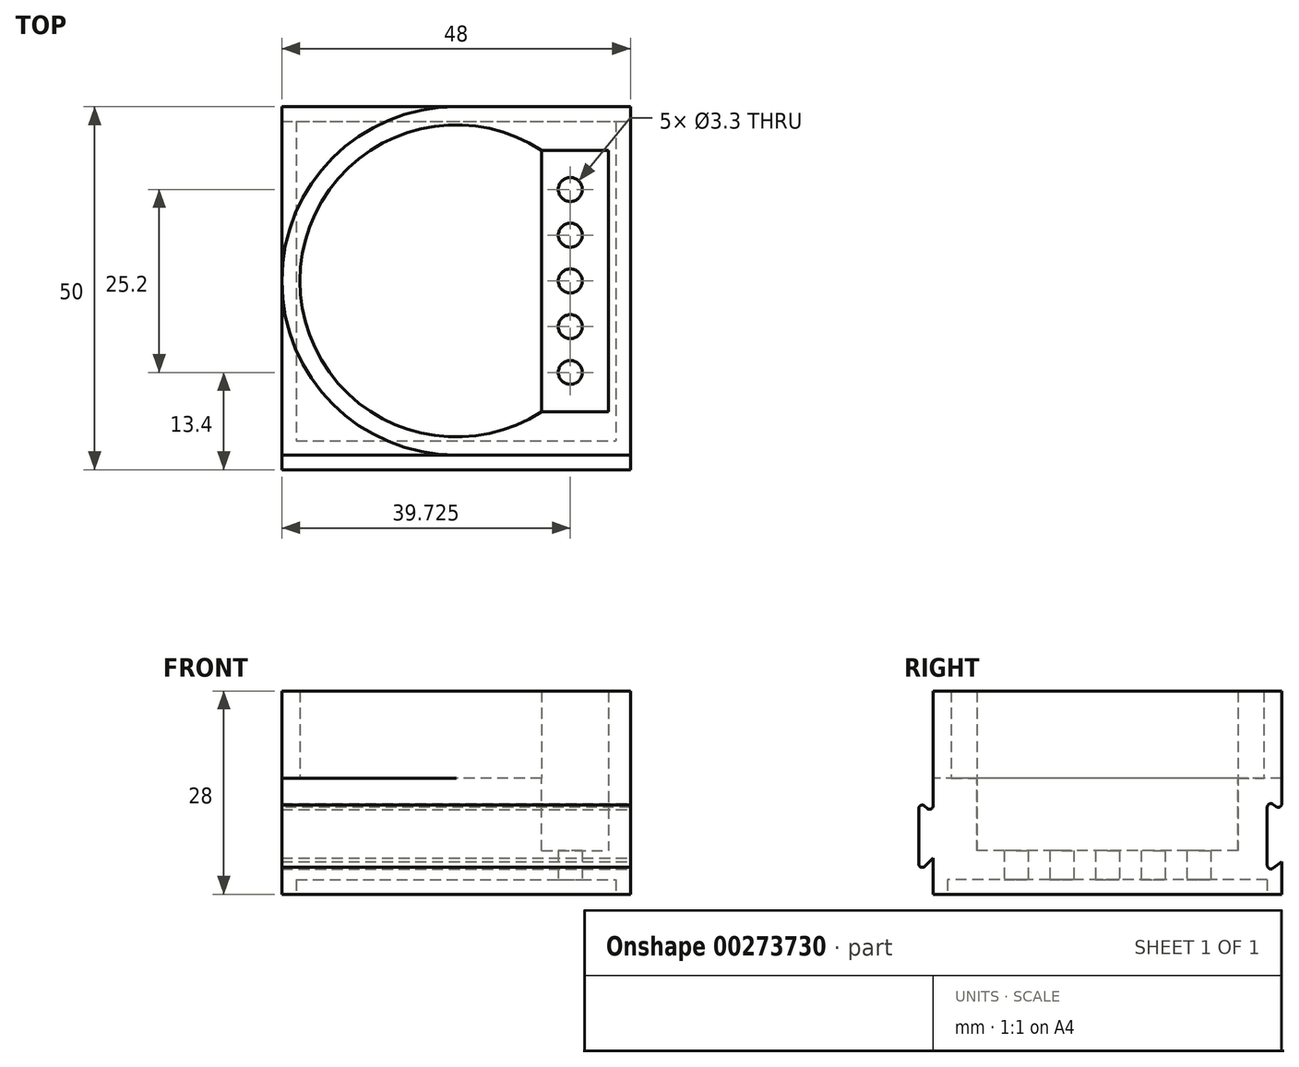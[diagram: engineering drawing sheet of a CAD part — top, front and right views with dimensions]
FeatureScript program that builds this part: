
annotation { "Feature Type Name" : "Feature", "Feature Type Description" : "" }
export const myFeature = defineFeature(function(context is Context, id is Id, definition is map)
    precondition{}
    {
        {
            var Q0;
            Q0=qCreatedBy(makeId("Top.planeOp"),FACE);
            var sketch = newSketch(context, id + "F0", { "sketchPlane" : qUnion([Q0])});
            skCircle(sketch, "E0", {"center": v(0, 0) * mm, "radius": 21.5 * mm});
            skCircle(sketch, "E1", {"center": v(0, 0) * mm, "radius": 24 * mm});
            skLineSegment(sketch, "E2.bottom", {"start": v(-24, 24) * mm, "end": v(24, 24) * mm});
            skLineSegment(sketch, "E2.top", {"start": v(-24, -24) * mm, "end": v(24, -24) * mm});
            skLineSegment(sketch, "E2.left", {"start": v(-24, 24) * mm, "end": v(-24, -24) * mm});
            skLineSegment(sketch, "E2.right", {"start": v(24, 24) * mm, "end": v(24, -24) * mm});
            skPoint(sketch, "E3", {"position": v(0, 24) * mm});
            skPoint(sketch, "E4", {"position": v(-24, 0) * mm});
            skLineSegment(sketch, "E5.bottom", {"start": v(11.76, 18) * mm, "end": v(20.96, 18) * mm});
            skLineSegment(sketch, "E5.top", {"start": v(11.76, -18) * mm, "end": v(20.96, -18) * mm});
            skLineSegment(sketch, "E5.left", {"start": v(11.76, 18) * mm, "end": v(11.76, -18) * mm});
            skLineSegment(sketch, "E5.right", {"start": v(20.96, 18) * mm, "end": v(20.96, -18) * mm});
            skLineSegment(sketch, "E6", {"start": v(20.96, -18) * mm, "end": v(20.96, -24) * mm, "construction": true});
            skLineSegment(sketch, "E7", {"start": v(20.96, 18) * mm, "end": v(20.96, 24) * mm, "construction": true});
            skCircle(sketch, "E8", {"center": v(0, 0) * mm, "radius": 20.15 * mm, "construction": true});
            skSolve(sketch);
        }
        {
            var Q0;
            Q0=makeQuery(id+"F0.imprint","IMPRINT",FACE,{"disambiguationData":[TD([[makeQuery(id+"F0.imprint","IMPRINT",EDGE,{"derivedFrom":sQuery(id+"F0.wireOp",EDGE,"E1")}),-1.0]])]});
            var Q1;
            Q1=makeQuery(id+"F0.imprint","IMPRINT",FACE,{"disambiguationData":[TD([[makeQuery(id+"F0.imprint","IMPRINT",EDGE,{"derivedFrom":sQuery(id+"F0.wireOp",EDGE,"E0")}),-1.0]])]});
            var Q2;
            {var subQ0=sQuery(id+"F0.wireOp",EDGE,"E1");var subQ4=makeQuery(id+"F0.imprint","INTERSECT",VERTEX,{"derivedFrom":[subQ0,sQuery(id+"F0.wireOp",EDGE,"E2.bottom")]});Q2=makeQuery(id+"F0.imprint","IMPRINT",FACE,{"disambiguationData":[TD([[makeQuery(id+"F0.imprint","IMPRINT",EDGE,{"disambiguationData":[TD([[subQ4,1.0]])],"derivedFrom":subQ0}),1.0]])]});}
            var Q3;
            {var subQ0=sQuery(id+"F0.wireOp",EDGE,"E2.bottom");var subQ1=sQuery(id+"F0.wireOp",EDGE,"E1");var subQ2=makeQuery(id+"F0.imprint","INTERSECT",VERTEX,{"derivedFrom":[subQ1,subQ0]});Q3=makeQuery(id+"F0.imprint","IMPRINT",FACE,{"disambiguationData":[TD([[makeQuery(id+"F0.imprint","IMPRINT",EDGE,{"disambiguationData":[TD([[subQ2,-1.0]])],"derivedFrom":subQ1}),-1.0]])]});}
            var Q4;
            {var subQ0=sQuery(id+"F0.wireOp",EDGE,"7gHcx121-CxHX-03ng-84u3-5FYPdPzAS1k3.top");Q4=makeQuery(id+"F0.imprint","IMPRINT",FACE,{"disambiguationData":[TD([[makeQuery(id+"F0.imprint","IMPRINT",EDGE,{"derivedFrom":subQ0}),1.0]])]});}
            var Q5;
            {var subQ2=sQuery(id+"F0.wireOp",EDGE,"7gHcx121-CxHX-03ng-84u3-5FYPdPzAS1k3.bottom");var subQ5=sQuery(id+"F0.wireOp",EDGE,"E0");var subQ6=makeQuery(id+"F0.imprint","INTERSECT",VERTEX,{"disambiguationData":[OD(0.0)],"derivedFrom":[subQ5,subQ2]});Q5=makeQuery(id+"F0.imprint","IMPRINT",FACE,{"disambiguationData":[TD([[makeQuery(id+"F0.imprint","IMPRINT",EDGE,{"disambiguationData":[TD([[subQ6,-1.0]])],"derivedFrom":subQ5}),-1.0]])]});}
            var Q6;
            {var subQ0=sQuery(id+"F0.wireOp",EDGE,"7gHcx121-CxHX-03ng-84u3-5FYPdPzAS1k3.bottom");var subQ1=sQuery(id+"F0.wireOp",EDGE,"E1");var subQ2=makeQuery(id+"F0.imprint","INTERSECT",VERTEX,{"disambiguationData":[OD(1.0)],"derivedFrom":[subQ1,subQ0]});Q6=makeQuery(id+"F0.imprint","IMPRINT",FACE,{"disambiguationData":[TD([[makeQuery(id+"F0.imprint","IMPRINT",EDGE,{"disambiguationData":[TD([[subQ2,-1.0]])],"derivedFrom":subQ1}),-1.0]])]});}
            var Q7;
            {var subQ0=sQuery(id+"F0.wireOp",EDGE,"7gHcx121-CxHX-03ng-84u3-5FYPdPzAS1k3.left");var subQ1=sQuery(id+"F0.wireOp",EDGE,"E1");var subQ2=makeQuery(id+"F0.imprint","INTERSECT",VERTEX,{"derivedFrom":[subQ1,subQ0]});Q7=makeQuery(id+"F0.imprint","IMPRINT",FACE,{"disambiguationData":[TD([[makeQuery(id+"F0.imprint","IMPRINT",EDGE,{"disambiguationData":[TD([[subQ2,-1.0]])],"derivedFrom":subQ1}),-1.0]])]});}
            var Q8;
            {var subQ0=sQuery(id+"F0.wireOp",EDGE,"E2.bottom");var subQ1=sQuery(id+"F0.wireOp",EDGE,"E1");var subQ2=makeQuery(id+"F0.imprint","INTERSECT",VERTEX,{"derivedFrom":[subQ1,subQ0]});Q8=makeQuery(id+"F0.imprint","IMPRINT",FACE,{"disambiguationData":[TD([[makeQuery(id+"F0.imprint","IMPRINT",EDGE,{"disambiguationData":[TD([[subQ2,1.0]])],"derivedFrom":subQ1}),-1.0]])]});}
            var Q9;
            {var subQ0=sQuery(id+"F0.wireOp",EDGE,"E5.left");Q9=makeQuery(id+"F0.imprint","IMPRINT",FACE,{"disambiguationData":[TD([[makeQuery(id+"F0.imprint","IMPRINT",EDGE,{"derivedFrom":subQ0}),-1.0]])]});}
            var Q10;
            {var subQ0=sQuery(id+"F0.wireOp",EDGE,"E2.left");var subQ1=sQuery(id+"F0.wireOp",EDGE,"E1");var subQ2=makeQuery(id+"F0.imprint","INTERSECT",VERTEX,{"derivedFrom":[subQ1,subQ0]});Q10=makeQuery(id+"F0.imprint","IMPRINT",FACE,{"disambiguationData":[TD([[makeQuery(id+"F0.imprint","IMPRINT",EDGE,{"disambiguationData":[TD([[subQ2,-1.0]])],"derivedFrom":subQ1}),-1.0]])]});}
            var Q11;
            {var subQ0=sQuery(id+"F0.wireOp",EDGE,"E5.right");var subQ1=sQuery(id+"F0.wireOp",EDGE,"E1");var subQ2=makeQuery(id+"F0.imprint","INTERSECT",VERTEX,{"disambiguationData":[OD(0.0)],"derivedFrom":[subQ1,subQ0]});Q11=makeQuery(id+"F0.imprint","IMPRINT",FACE,{"disambiguationData":[TD([[makeQuery(id+"F0.imprint","IMPRINT",EDGE,{"disambiguationData":[TD([[subQ2,-1.0]])],"derivedFrom":subQ1}),-1.0]])]});}
            var Q12;
            {var subQ0=sQuery(id+"F0.wireOp",EDGE,"E5.top");var subQ1=sQuery(id+"F0.wireOp",EDGE,"E1");var subQ2=makeQuery(id+"F0.imprint","INTERSECT",VERTEX,{"derivedFrom":[subQ1,subQ0]});Q12=makeQuery(id+"F0.imprint","IMPRINT",FACE,{"disambiguationData":[TD([[makeQuery(id+"F0.imprint","IMPRINT",EDGE,{"disambiguationData":[TD([[subQ2,-1.0]])],"derivedFrom":subQ1}),-1.0]])]});}
            var Q13;
            {var subQ0=sQuery(id+"F0.wireOp",EDGE,"E5.right");var subQ1=sQuery(id+"F0.wireOp",EDGE,"E0");var subQ2=makeQuery(id+"F0.imprint","INTERSECT",VERTEX,{"disambiguationData":[OD(0.0)],"derivedFrom":[subQ1,subQ0]});Q13=makeQuery(id+"F0.imprint","IMPRINT",FACE,{"disambiguationData":[TD([[makeQuery(id+"F0.imprint","IMPRINT",EDGE,{"disambiguationData":[TD([[subQ2,1.0]])],"derivedFrom":subQ1}),1.0]])]});}
            var Q14;
            {var subQ0=sQuery(id+"F0.wireOp",EDGE,"E5.left");Q14=makeQuery(id+"F0.imprint","IMPRINT",FACE,{"disambiguationData":[TD([[makeQuery(id+"F0.imprint","IMPRINT",EDGE,{"derivedFrom":subQ0}),1.0]])]});}
            var Q15;
            {var subQ0=sQuery(id+"F0.wireOp",EDGE,"E5.right");var subQ1=sQuery(id+"F0.wireOp",EDGE,"E0");var subQ2=makeQuery(id+"F0.imprint","INTERSECT",VERTEX,{"disambiguationData":[OD(0.0)],"derivedFrom":[subQ1,subQ0]});Q15=makeQuery(id+"F0.imprint","IMPRINT",FACE,{"disambiguationData":[TD([[makeQuery(id+"F0.imprint","IMPRINT",EDGE,{"disambiguationData":[TD([[subQ2,1.0]])],"derivedFrom":subQ1}),-1.0]])]});}
            var Q16;
            {var subQ0=sQuery(id+"F0.wireOp",EDGE,"E1");var subQ1=makeQuery(id+"F0.imprint","INTERSECT",VERTEX,{"derivedFrom":[subQ0,sQuery(id+"F0.wireOp",EDGE,"E2.right")]});Q16=makeQuery(id+"F0.imprint","IMPRINT",FACE,{"disambiguationData":[TD([[makeQuery(id+"F0.imprint","IMPRINT",EDGE,{"disambiguationData":[TD([[subQ1,-1.0]])],"derivedFrom":subQ0}),1.0]])]});}
            extrude(context, id + "F1", {"entities" : qUnion([Q0, Q1, Q2, Q3, Q4, Q5, Q6, Q7, Q8, Q9, Q10, Q11, Q12, Q13, Q14, Q15, Q16]), "oppositeDirection" : true, "depth" : 16 * mm});
        }
        {
            var Q0;
            {var subQ0=sQuery(id+"F0.wireOp",EDGE,"E1");var subQ4=makeQuery(id+"F0.imprint","INTERSECT",VERTEX,{"derivedFrom":[subQ0,sQuery(id+"F0.wireOp",EDGE,"E2.bottom")]});Q0=makeQuery(id+"F0.imprint","IMPRINT",FACE,{"disambiguationData":[TD([[makeQuery(id+"F0.imprint","IMPRINT",EDGE,{"disambiguationData":[TD([[subQ4,1.0]])],"derivedFrom":subQ0}),1.0]])]});}
            var Q1;
            {var subQ1=sQuery(id+"F0.wireOp",EDGE,"E2.top");var subQ3=sQuery(id+"F0.wireOp",EDGE,"E1");var subQ4=makeQuery(id+"F0.imprint","INTERSECT",VERTEX,{"derivedFrom":[subQ3,subQ1]});Q1=makeQuery(id+"F0.imprint","IMPRINT",FACE,{"disambiguationData":[TD([[makeQuery(id+"F0.imprint","IMPRINT",EDGE,{"disambiguationData":[TD([[subQ4,-1.0]])],"derivedFrom":subQ3}),-1.0]])]});}
            var Q2;
            {var subQ0=sQuery(id+"F0.wireOp",EDGE,"E5.right");var subQ1=sQuery(id+"F0.wireOp",EDGE,"E0");var subQ2=makeQuery(id+"F0.imprint","INTERSECT",VERTEX,{"disambiguationData":[OD(0.0)],"derivedFrom":[subQ1,subQ0]});Q2=makeQuery(id+"F0.imprint","IMPRINT",FACE,{"disambiguationData":[TD([[makeQuery(id+"F0.imprint","IMPRINT",EDGE,{"disambiguationData":[TD([[subQ2,1.0]])],"derivedFrom":subQ1}),-1.0]])]});}
            var Q3;
            {var subQ0=sQuery(id+"F0.wireOp",EDGE,"E2.right");var subQ3=sQuery(id+"F0.wireOp",EDGE,"E1");var subQ4=makeQuery(id+"F0.imprint","INTERSECT",VERTEX,{"derivedFrom":[subQ3,subQ0]});Q3=makeQuery(id+"F0.imprint","IMPRINT",FACE,{"disambiguationData":[TD([[makeQuery(id+"F0.imprint","IMPRINT",EDGE,{"disambiguationData":[TD([[subQ4,-1.0]])],"derivedFrom":subQ3}),-1.0]])]});}
            var Q4;
            {var subQ0=sQuery(id+"F0.wireOp",EDGE,"E5.right");var subQ1=sQuery(id+"F0.wireOp",EDGE,"E0");var subQ2=makeQuery(id+"F0.imprint","INTERSECT",VERTEX,{"disambiguationData":[OD(0.0)],"derivedFrom":[subQ1,subQ0]});Q4=makeQuery(id+"F0.imprint","IMPRINT",FACE,{"disambiguationData":[TD([[makeQuery(id+"F0.imprint","IMPRINT",EDGE,{"disambiguationData":[TD([[subQ2,1.0]])],"derivedFrom":subQ1}),1.0]])]});}
            var Q5;
            {var subQ0=sQuery(id+"F0.wireOp",EDGE,"E1");var subQ1=makeQuery(id+"F0.imprint","INTERSECT",VERTEX,{"derivedFrom":[subQ0,sQuery(id+"F0.wireOp",EDGE,"E2.right")]});Q5=makeQuery(id+"F0.imprint","IMPRINT",FACE,{"disambiguationData":[TD([[makeQuery(id+"F0.imprint","IMPRINT",EDGE,{"disambiguationData":[TD([[subQ1,-1.0]])],"derivedFrom":subQ0}),1.0]])]});}
            extrude(context, id + "F2", {"entities" : qUnion([Q0, Q1, Q2, Q3, Q4, Q5]), "operationType" : NewBodyOperationType.ADD, "depth" : 12 * mm});
        }
        {
            var Q0;
            Q0=makeQuery(id+"F1.opExtrude","CAP_FACE",FACE,{"disambiguationData":[OSD([sQuery(id+"F0.wireOp",EDGE,"E2.bottom"),sQuery(id+"F0.wireOp",EDGE,"E2.top"),sQuery(id+"F0.wireOp",EDGE,"E2.left"),sQuery(id+"F0.wireOp",EDGE,"E2.right")])],"isStart":false});
            var sketch = newSketch(context, id + "F3", { "sketchPlane" : qUnion([Q0])});
            skLineSegment(sketch, "E9.0", {"start": v(-22, 22) * mm, "end": v(22, 22) * mm});
            skLineSegment(sketch, "E9.1", {"start": v(-22, -22) * mm, "end": v(-22, 22) * mm});
            skLineSegment(sketch, "E9.2", {"start": v(-22, -22) * mm, "end": v(22, -22) * mm});
            skLineSegment(sketch, "E9.3", {"start": v(22, -22) * mm, "end": v(22, 22) * mm});
            skSolve(sketch);
        }
        {
            var Q0;
            Q0=makeQuery(id+"F3.imprint","IMPRINT",FACE,{"disambiguationData":[TD([[makeQuery(id+"F3.imprint","IMPRINT",EDGE,{"derivedFrom":sQuery(id+"F3.wireOp",EDGE,"E9.0")}),-1.0]])]});
            var Q1;
            {var subQ0=sQuery(id+"F0.wireOp",EDGE,"E2.right");var subQ1=sQuery(id+"F0.wireOp",EDGE,"E2.left");var subQ2=sQuery(id+"F0.wireOp",EDGE,"E2.top");var subQ3=sQuery(id+"F0.wireOp",EDGE,"E2.bottom");Q1=makeQuery(id+"F2.boolean.opBoolean","SPLIT",FACE,{"disambiguationData":[TD([makeQuery(id+"F1.opExtrude","SWEPT_FACE",FACE,{"disambiguationData":[OSD([subQ3])]})])],"derivedFrom":makeQuery(id+"F1.opExtrude","CAP_FACE",FACE,{"disambiguationData":[OSD([subQ3,subQ2,subQ1,subQ0])],"isStart":true})});}
            extrude(context, id + "F4", {"entities" : qUnion([Q0]), "operationType" : NewBodyOperationType.REMOVE, "oppositeDirection" : true, "endBoundEntityFace" : qUnion([Q1]), "depth" : 2 * mm});
        }
        {
            var Q0;
            Q0=makeQuery(id+"F4.boolean.opBoolean","COPY",FACE,{"derivedFrom":makeQuery(id+"F4.opExtrude","CAP_FACE",FACE,{"disambiguationData":[OSD([sQuery(id+"F3.wireOp",EDGE,"E9.0"),sQuery(id+"F3.wireOp",EDGE,"E9.1"),sQuery(id+"F3.wireOp",EDGE,"E9.2"),sQuery(id+"F3.wireOp",EDGE,"E9.3")])],"isStart":false})});
            var sketch = newSketch(context, id + "F5", { "sketchPlane" : qUnion([Q0])});
            skLineSegment(sketch, "E10.0", {"start": v(11.76, -18) * mm, "end": v(20.96, -18) * mm});
            skLineSegment(sketch, "E10.1", {"start": v(11.76, 18) * mm, "end": v(20.96, 18) * mm});
            skLineSegment(sketch, "E10.2", {"start": v(20.96, -18) * mm, "end": v(20.96, 18) * mm});
            skLineSegment(sketch, "E10.3", {"start": v(11.76, -18) * mm, "end": v(11.76, 18) * mm});
            skCircle(sketch, "E11", {"center": v(15.72, -12.6) * mm, "radius": 1.65 * mm});
            skCircle(sketch, "E12.0.1.0", {"center": v(15.72, -6.3) * mm, "radius": 1.65 * mm});
            skCircle(sketch, "E12.0.2.0", {"center": v(15.72, 0) * mm, "radius": 1.65 * mm});
            skCircle(sketch, "E12.0.3.0", {"center": v(15.72, 6.3) * mm, "radius": 1.65 * mm});
            skCircle(sketch, "E12.0.4.0", {"center": v(15.72, 12.6) * mm, "radius": 1.65 * mm});
            skLineSegment(sketch, "E12.direction1", {"start": v(15.72, -12.6) * mm, "end": v(40.72, -12.6) * mm, "construction": true});
            skLineSegment(sketch, "E12.direction2", {"start": v(15.72, -12.6) * mm, "end": v(15.72, -6.3) * mm, "construction": true});
            skCircle(sketch, "E13.0", {"center": v(0, 0) * mm, "radius": 21.5 * mm});
            skCircle(sketch, "E14.0", {"center": v(0, 0) * mm, "radius": 20.15 * mm, "construction": true});
            skSolve(sketch);
        }
        {
            var Q0;
            {var subQ0=sQuery(id+"F5.wireOp",EDGE,"E13.0");var subQ1=sQuery(id+"F5.wireOp",EDGE,"E12.0.4.0");var subQ2=makeQuery(id+"F5.imprint","INTERSECT",VERTEX,{"disambiguationData":[OD(0.0)],"derivedFrom":[subQ1,subQ0]});Q0=makeQuery(id+"F5.imprint","IMPRINT",FACE,{"disambiguationData":[TD([[makeQuery(id+"F5.imprint","IMPRINT",EDGE,{"disambiguationData":[TD([[subQ2,1.0]])],"derivedFrom":subQ1}),1.0]])]});}
            var Q1;
            {var subQ0=sQuery(id+"F5.wireOp",EDGE,"E13.0");var subQ1=sQuery(id+"F5.wireOp",EDGE,"E12.0.4.0");var subQ2=makeQuery(id+"F5.imprint","INTERSECT",VERTEX,{"disambiguationData":[OD(0.0)],"derivedFrom":[subQ1,subQ0]});Q1=makeQuery(id+"F5.imprint","IMPRINT",FACE,{"disambiguationData":[TD([[makeQuery(id+"F5.imprint","IMPRINT",EDGE,{"disambiguationData":[TD([[subQ2,-1.0]])],"derivedFrom":subQ1}),1.0]])]});}
            var Q2;
            Q2=makeQuery(id+"F5.imprint","IMPRINT",FACE,{"disambiguationData":[TD([[makeQuery(id+"F5.imprint","IMPRINT",EDGE,{"derivedFrom":sQuery(id+"F5.wireOp",EDGE,"E12.0.3.0")}),1.0]])]});
            var Q3;
            Q3=makeQuery(id+"F5.imprint","IMPRINT",FACE,{"disambiguationData":[TD([[makeQuery(id+"F5.imprint","IMPRINT",EDGE,{"derivedFrom":sQuery(id+"F5.wireOp",EDGE,"E12.0.2.0")}),1.0]])]});
            var Q4;
            Q4=makeQuery(id+"F5.imprint","IMPRINT",FACE,{"disambiguationData":[TD([[makeQuery(id+"F5.imprint","IMPRINT",EDGE,{"derivedFrom":sQuery(id+"F5.wireOp",EDGE,"E12.0.1.0")}),1.0]])]});
            var Q5;
            {var subQ0=sQuery(id+"F5.wireOp",EDGE,"E13.0");var subQ1=sQuery(id+"F5.wireOp",EDGE,"E11");var subQ2=makeQuery(id+"F5.imprint","INTERSECT",VERTEX,{"disambiguationData":[OD(0.0)],"derivedFrom":[subQ1,subQ0]});Q5=makeQuery(id+"F5.imprint","IMPRINT",FACE,{"disambiguationData":[TD([[makeQuery(id+"F5.imprint","IMPRINT",EDGE,{"disambiguationData":[TD([[subQ2,-1.0]])],"derivedFrom":subQ1}),1.0]])]});}
            var Q6;
            {var subQ0=sQuery(id+"F5.wireOp",EDGE,"E13.0");var subQ1=sQuery(id+"F5.wireOp",EDGE,"E11");var subQ2=makeQuery(id+"F5.imprint","INTERSECT",VERTEX,{"disambiguationData":[OD(0.0)],"derivedFrom":[subQ1,subQ0]});Q6=makeQuery(id+"F5.imprint","IMPRINT",FACE,{"disambiguationData":[TD([[makeQuery(id+"F5.imprint","IMPRINT",EDGE,{"disambiguationData":[TD([[subQ2,1.0]])],"derivedFrom":subQ1}),1.0]])]});}
            extrude(context, id + "F6", {"entities" : qUnion([Q0, Q1, Q2, Q3, Q4, Q5, Q6]), "operationType" : NewBodyOperationType.REMOVE, "oppositeDirection" : true, "depth" : 25 * mm});
        }
        {
            var Q0;
            Q0=makeQuery(id+"F1.opExtrude","SWEPT_FACE",FACE,{"disambiguationData":[OSD([sQuery(id+"F0.wireOp",EDGE,"E2.right")])]});
            var sketch = newSketch(context, id + "F7", { "sketchPlane" : qUnion([Q0])});
            skLineSegment(sketch, "E15", {"start": v(-24, -11) * mm, "end": v(-26, -13) * mm});
            skLineSegment(sketch, "E16", {"start": v(-26, -13) * mm, "end": v(-26, -3) * mm});
            skLineSegment(sketch, "E17", {"start": v(-26, -3) * mm, "end": v(-24, -5) * mm});
            skLineSegment(sketch, "E18", {"start": v(22, -16) * mm, "end": v(24, -16) * mm});
            skLineSegment(sketch, "E19", {"start": v(22, -16) * mm, "end": v(22, 0) * mm, "construction": true});
            skLineSegment(sketch, "E20", {"start": v(24, 0) * mm, "end": v(22, 0) * mm});
            skLineSegment(sketch, "E21", {"start": v(24, -11.5) * mm, "end": v(22, -13) * mm});
            skLineSegment(sketch, "E22", {"start": v(22, -3) * mm, "end": v(24, -4.5) * mm});
            skLineSegment(sketch, "E23", {"start": v(24, -8) * mm, "end": v(-24, -8) * mm, "construction": true});
            skLineSegment(sketch, "E24", {"start": v(-24, -5) * mm, "end": v(-24, -8) * mm, "construction": true});
            skLineSegment(sketch, "E25", {"start": v(-24, -8) * mm, "end": v(-24, -11) * mm, "construction": true});
            skLineSegment(sketch, "E26", {"start": v(24, 0) * mm, "end": v(24, -16) * mm, "construction": true});
            skLineSegment(sketch, "E27", {"start": v(-24, 0) * mm, "end": v(-24, -16) * mm, "construction": true});
            skPoint(sketch, "E28", {"position": v(-24, -8) * mm});
            skLineSegment(sketch, "E29", {"start": v(22, -3) * mm, "end": v(22, -13) * mm, "construction": true});
            skPoint(sketch, "E30", {"position": v(22, -8) * mm});
            skLineSegment(sketch, "E31", {"start": v(22, -3) * mm, "end": v(22, -13) * mm});
            skSolve(sketch);
        }
        {
            var Q0;
            {var subQ0=sQuery(id+"F7.wireOp",EDGE,"E15");Q0=makeQuery(id+"F7.imprint","IMPRINT",FACE,{"disambiguationData":[TD([[makeQuery(id+"F7.imprint","IMPRINT",EDGE,{"derivedFrom":subQ0}),-1.0]])]});}
            var Q1;
            {var subQ0=sQuery(id+"F7.wireOp",EDGE,"E18");Q1=makeQuery(id+"F7.imprint","IMPRINT",FACE,{"disambiguationData":[TD([[makeQuery(id+"F7.imprint","IMPRINT",EDGE,{"derivedFrom":subQ0}),1.0]])]});}
            var Q2;
            {var subQ0=sQuery(id+"F7.wireOp",EDGE,"E20");Q2=makeQuery(id+"F7.imprint","IMPRINT",FACE,{"disambiguationData":[TD([[makeQuery(id+"F7.imprint","IMPRINT",EDGE,{"derivedFrom":subQ0}),1.0]])]});}
            var Q3;
            Q3=makeQuery(id+"F1.opExtrude","SWEPT_FACE",FACE,{"disambiguationData":[OSD([sQuery(id+"F0.wireOp",EDGE,"E2.left")])]});
            extrude(context, id + "F8", {"entities" : qUnion([Q0, Q1, Q2]), "operationType" : NewBodyOperationType.ADD, "endBound" : BoundingType.UP_TO_SURFACE, "oppositeDirection" : true, "endBoundEntityFace" : qUnion([Q3]), "depth" : 25 * mm});
        }
        {
            var Q0;
            {var subQ0=sQuery(id+"F7.wireOp",EDGE,"E21");Q0=makeQuery(id+"F7.imprint","IMPRINT",FACE,{"disambiguationData":[TD([[makeQuery(id+"F7.imprint","IMPRINT",EDGE,{"derivedFrom":subQ0}),-1.0]])]});}
            var Q1;
            {var subQ0=sQuery(id+"F0.wireOp",EDGE,"E2.left");Q1=makeQuery(id+"F8.boolean.opBoolean","MERGE",FACE,{"derivedFrom":[makeQuery(id+"F1.opExtrude","SWEPT_FACE",FACE,{"disambiguationData":[OSD([subQ0])]}),makeQuery(id+"F8.opExtrude","CAP_FACE",FACE,{"disambiguationData":[OSD([subQ0])],"isStart":false})]});}
            extrude(context, id + "F9", {"entities" : qUnion([Q0]), "operationType" : NewBodyOperationType.REMOVE, "endBound" : BoundingType.UP_TO_SURFACE, "oppositeDirection" : true, "endBoundEntityFace" : qUnion([Q1]), "depth" : 25 * mm});
        }
        {
            var Q0;
            Q0=makeQuery(id+"F8.opExtrude","SWEPT_EDGE",EDGE,{"disambiguationData":[OSD([sQuery(id+"F0.wireOp",EDGE,"E2.top"),sQuery(id+"F0.wireOp",EDGE,"E2.right"),sQuery(id+"F7.wireOp",EDGE,"E15")])]});
            var Q1;
            Q1=makeQuery(id+"F8.opExtrude","SWEPT_EDGE",EDGE,{"disambiguationData":[OSD([sQuery(id+"F7.wireOp",EDGE,"E15"),sQuery(id+"F7.wireOp",EDGE,"E16")])]});
            var Q2;
            Q2=makeQuery(id+"F8.opExtrude","SWEPT_EDGE",EDGE,{"disambiguationData":[OSD([sQuery(id+"F7.wireOp",EDGE,"E16"),sQuery(id+"F7.wireOp",EDGE,"E17")])]});
            var Q3;
            Q3=makeQuery(id+"F8.opExtrude","SWEPT_EDGE",EDGE,{"disambiguationData":[OSD([sQuery(id+"F0.wireOp",EDGE,"E2.top"),sQuery(id+"F0.wireOp",EDGE,"E2.right"),sQuery(id+"F7.wireOp",EDGE,"E17")])]});
            var Q4;
            Q4=makeQuery(id+"F8.opExtrude","SWEPT_EDGE",EDGE,{"disambiguationData":[OSD([sQuery(id+"F0.wireOp",EDGE,"E2.bottom"),sQuery(id+"F0.wireOp",EDGE,"E2.right"),sQuery(id+"F7.wireOp",EDGE,"vTmjsysW-Mem8-C94P-BJdX-mGUMZyO6RJHl"),sQuery(id+"F7.wireOp",EDGE,"E22")])]});
            var Q5;
            Q5=makeQuery(id+"F8.opExtrude","SWEPT_EDGE",EDGE,{"disambiguationData":[OSD([sQuery(id+"F7.wireOp",EDGE,"E19"),sQuery(id+"F7.wireOp",EDGE,"E22")])]});
            var Q6;
            Q6=makeQuery(id+"F8.opExtrude","SWEPT_EDGE",EDGE,{"disambiguationData":[OSD([sQuery(id+"F0.wireOp",EDGE,"E2.bottom"),sQuery(id+"F0.wireOp",EDGE,"E2.right"),sQuery(id+"F7.wireOp",EDGE,"E21"),sQuery(id+"F7.wireOp",EDGE,"vTmjsysW-Mem8-C94P-BJdX-mGUMZyO6RJHl")])]});
            var Q7;
            Q7=makeQuery(id+"F8.opExtrude","SWEPT_EDGE",EDGE,{"disambiguationData":[OSD([sQuery(id+"F7.wireOp",EDGE,"E19"),sQuery(id+"F7.wireOp",EDGE,"E21")])]});
            var Q8;
            Q8=makeQuery(id+"F9.boolean.opBoolean","COPY",EDGE,{"derivedFrom":makeQuery(id+"F9.opExtrude","SWEPT_EDGE",EDGE,{"disambiguationData":[OSD([sQuery(id+"F0.wireOp",EDGE,"E2.bottom"),sQuery(id+"F0.wireOp",EDGE,"E2.right"),sQuery(id+"F7.wireOp",EDGE,"E22")])]})});
            var Q9;
            Q9=makeQuery(id+"F9.boolean.opBoolean","COPY",EDGE,{"derivedFrom":makeQuery(id+"F9.opExtrude","SWEPT_EDGE",EDGE,{"disambiguationData":[OSD([sQuery(id+"F0.wireOp",EDGE,"E2.bottom"),sQuery(id+"F0.wireOp",EDGE,"E2.right"),sQuery(id+"F7.wireOp",EDGE,"E21")])]})});
            var Q10;
            Q10=makeQuery(id+"F9.boolean.opBoolean","COPY",EDGE,{"derivedFrom":makeQuery(id+"F9.opExtrude","SWEPT_EDGE",EDGE,{"disambiguationData":[OSD([sQuery(id+"F7.wireOp",EDGE,"E21"),sQuery(id+"F7.wireOp",EDGE,"E31")])]})});
            var Q11;
            Q11=makeQuery(id+"F9.boolean.opBoolean","COPY",EDGE,{"derivedFrom":makeQuery(id+"F9.opExtrude","SWEPT_EDGE",EDGE,{"disambiguationData":[OSD([sQuery(id+"F7.wireOp",EDGE,"E22"),sQuery(id+"F7.wireOp",EDGE,"E31")])]})});
            fillet(context, id + "F10", {"entities" : qUnion([Q0, Q1, Q2, Q3, Q4, Q5, Q6, Q7, Q8, Q9, Q10, Q11]), "radius" : 0.5 * mm, "tangentPropagation" : true, "allowEdgeOverflow" : false});
        }
        {
            var Q0;
            Q0=qCreatedBy(makeId("Front.planeOp"),FACE);
            var sketch = newSketch(context, id + "F11", { "sketchPlane" : qUnion([Q0])});
            skLineSegment(sketch, "E32.0", {"start": v(11.76, 12) * mm, "end": v(-21.5, 12) * mm});
            skLineSegment(sketch, "E33", {"start": v(11.76, 4) * mm, "end": v(11.76, 12) * mm, "construction": true});
            skLineSegment(sketch, "E34", {"start": v(11.76, 4) * mm, "end": v(13.56, 4) * mm});
            skLineSegment(sketch, "E35", {"start": v(13.56, 4) * mm, "end": v(13.56, 6.1) * mm});
            skLineSegment(sketch, "E36", {"start": v(13.56, 6.1) * mm, "end": v(11.76, 6.1) * mm});
            skLineSegment(sketch, "E37", {"start": v(11.76, 4) * mm, "end": v(11.76, 6.1) * mm});
            skSolve(sketch);
        }
        {
            var Q0;
            Q0=makeQuery(id+"F11.imprint","IMPRINT",FACE,{"disambiguationData":[TD([[makeQuery(id+"F11.imprint","IMPRINT",EDGE,{"derivedFrom":sQuery(id+"F11.wireOp",EDGE,"E34")}),1.0]])]});
            var Q1;
            Q1=makeQuery(id+"F2.opExtrude","CAP_EDGE",EDGE,{"disambiguationData":[OSD([sQuery(id+"F0.wireOp",EDGE,"E0")])],"isStart":false});
            revolve(context, id + "F12", {"operationType" : NewBodyOperationType.REMOVE, "entities" : qUnion([Q0]), "axis" : qUnion([Q1]), "revolveType" : RevolveType.FULL, "oppositeDirection" : true});
        }
        {
            var Q0;
            Q0=makeQuery(id+"F0.imprint","IMPRINT",FACE,{"disambiguationData":[TD([[makeQuery(id+"F0.imprint","IMPRINT",EDGE,{"derivedFrom":sQuery(id+"F0.wireOp",EDGE,"E0")}),1.0]])]});
            var sketch = newSketch(context, id + "F13", { "sketchPlane" : qUnion([Q0])});
            skLineSegment(sketch, "E38.0", {"start": v(11.76, 18) * mm, "end": v(11.76, -18) * mm});
            skLineSegment(sketch, "E39.0", {"start": v(11.76, -18) * mm, "end": v(20.96, -18) * mm});
            skLineSegment(sketch, "E39.1", {"start": v(20.96, 18) * mm, "end": v(20.96, -18) * mm});
            skLineSegment(sketch, "E39.2", {"start": v(11.76, 18) * mm, "end": v(20.96, 18) * mm});
            skSolve(sketch);
        }
        {
            var Q0;
            {var subQ0=sQuery(id+"F13.wireOp",EDGE,"I3hiSPsl-ye32-Vx4m-YmXu-QkAHstFrcVJg");var subQ1=sQuery(id+"F13.wireOp",EDGE,"4396e451-b7c7-415e-8e4c-47104f540c8e.0");var subQ2=makeQuery(id+"F13.imprint","INTERSECT",VERTEX,{"derivedFrom":[subQ1,subQ0]});Q0=makeQuery(id+"F13.imprint","IMPRINT",FACE,{"disambiguationData":[TD([[makeQuery(id+"F13.imprint","IMPRINT",EDGE,{"disambiguationData":[TD([[subQ2,-1.0]])],"derivedFrom":subQ1}),1.0]])]});}
            var Q1;
            {var subQ0=sQuery(id+"F0.wireOp",EDGE,"E5.left");Q1=makeQuery(id+"F0.imprint","IMPRINT",FACE,{"disambiguationData":[TD([[makeQuery(id+"F0.imprint","IMPRINT",EDGE,{"derivedFrom":subQ0}),1.0]])]});}
            var Q2;
            {var subQ0=sQuery(id+"F0.wireOp",EDGE,"E5.top");var subQ5=sQuery(id+"F0.wireOp",EDGE,"E1");var subQ6=makeQuery(id+"F0.imprint","INTERSECT",VERTEX,{"derivedFrom":[subQ5,subQ0]});Q2=makeQuery(id+"F0.imprint","IMPRINT",FACE,{"disambiguationData":[TD([[makeQuery(id+"F0.imprint","IMPRINT",EDGE,{"disambiguationData":[TD([[subQ6,-1.0]])],"derivedFrom":subQ5}),1.0]])]});}
            var Q3;
            {var subQ3=sQuery(id+"F13.wireOp",EDGE,"E39.2");Q3=makeQuery(id+"F13.imprint","IMPRINT",FACE,{"disambiguationData":[TD([[makeQuery(id+"F13.imprint","IMPRINT",EDGE,{"derivedFrom":subQ3}),-1.0]])]});}
            var Q4;
            {var subQ0=sQuery(id+"F0.wireOp",EDGE,"E5.top");var subQ1=sQuery(id+"F0.wireOp",EDGE,"E1");var subQ2=makeQuery(id+"F0.imprint","INTERSECT",VERTEX,{"derivedFrom":[subQ1,subQ0]});Q4=makeQuery(id+"F0.imprint","IMPRINT",FACE,{"disambiguationData":[TD([[makeQuery(id+"F0.imprint","IMPRINT",EDGE,{"disambiguationData":[TD([[subQ2,-1.0]])],"derivedFrom":subQ1}),-1.0]])]});}
            extrude(context, id + "F14", {"entities" : qUnion([Q0, Q1, Q2, Q3, Q4]), "operationType" : NewBodyOperationType.REMOVE, "oppositeDirection" : true, "depth" : 10 * mm});
        }
    });
